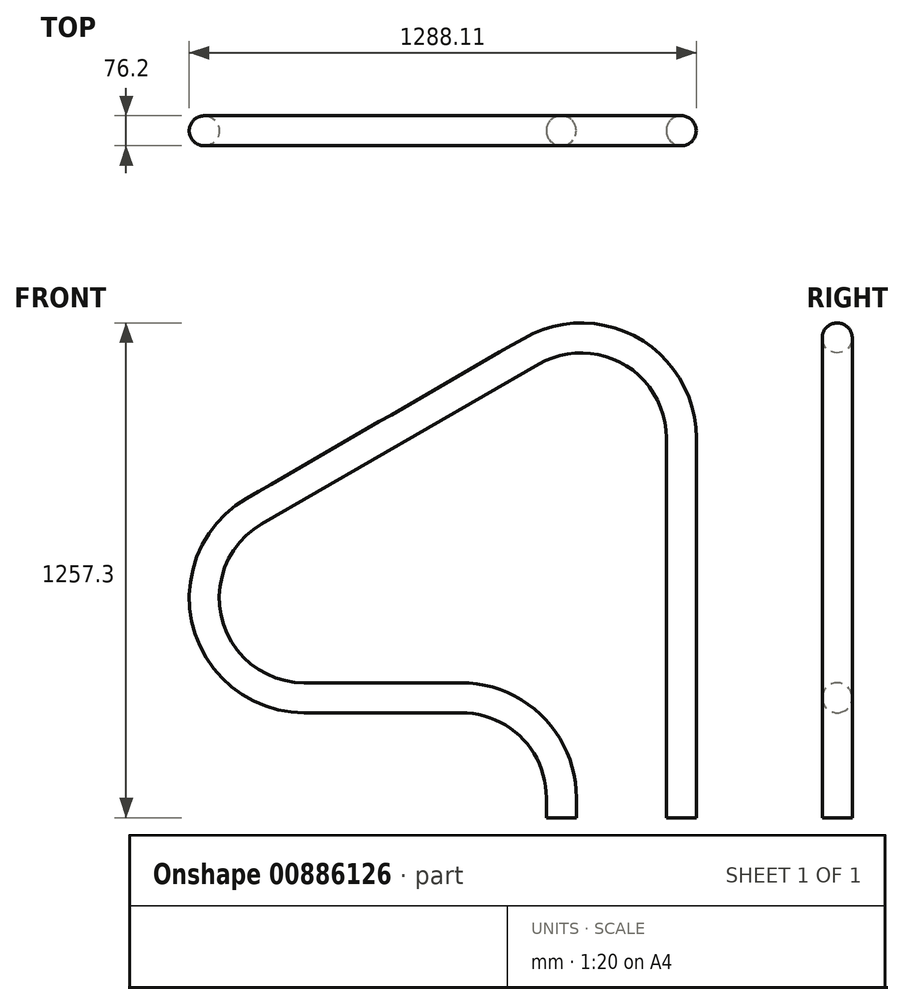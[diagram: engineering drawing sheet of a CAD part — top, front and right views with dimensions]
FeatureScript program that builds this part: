
annotation { "Feature Type Name" : "Feature", "Feature Type Description" : "" }
export const myFeature = defineFeature(function(context is Context, id is Id, definition is map)
    precondition{}
    {
        {
            var Q0;
            Q0=qCreatedBy(makeId("Front.planeOp"),FACE);
            var sketch = newSketch(context, id + "F0", { "sketchPlane" : qUnion([Q0])});
            skLineSegment(sketch, "E0", {"start": v(0, 0) * mm, "end": v(0, 965.2) * mm});
            skLineSegment(sketch, "E1", {"start": v(-381, 1185.17) * mm, "end": v(-1084.9, 778.77) * mm});
            skLineSegment(sketch, "E2", {"start": v(-957.9, 304.8) * mm, "end": v(-558.8, 304.8) * mm});
            skLineSegment(sketch, "E3", {"start": v(-304.8, 50.8) * mm, "end": v(-304.8, 0) * mm});
            skPoint(sketch, "E4.visualSharp", {"position": v(0, 1405.14) * mm});
            skArc(sketch, "E4.filletArc", {"start": v(0, 965.2) * mm, "mid": v(-127, 1185.17) * mm, "end": v(-381, 1185.17) * mm});
            skPoint(sketch, "E5.visualSharp", {"position": v(-1905.85, 304.8) * mm});
            skArc(sketch, "E5.filletArc", {"start": v(-1084.9, 778.77) * mm, "mid": v(-1203.25, 493.06) * mm, "end": v(-957.9, 304.8) * mm});
            skPoint(sketch, "E6.visualSharp", {"position": v(-304.8, 304.8) * mm});
            skArc(sketch, "E6.filletArc", {"start": v(-304.8, 50.8) * mm, "mid": v(-379.2, 230.4) * mm, "end": v(-558.8, 304.8) * mm});
            skLineSegment(sketch, "E7", {"start": v(-615.1, 1219.2) * mm, "end": v(-254, 1219.2) * mm, "construction": true});
            skSolve(sketch);
        }
        {
            var Q0;
            Q0=sQuery(id+"F0.wireOp",VERTEX,"E0.start");
            var Q1;
            Q1=sQuery(id+"F0.wireOp",EDGE,"E0");
            cPlane(context, id + "F1", {"entities" : qUnion([Q0, Q1]), "cplaneType" : CPlaneType.LINE_POINT, "offset" : 25.4 * mm, "width" : 152.4 * mm, "height" : 152.4 * mm});
        }
        {
            var Q0;
            Q0=qCreatedBy(id+"F1.planeOp",FACE);
            var sketch = newSketch(context, id + "F2", { "sketchPlane" : qUnion([Q0])});
            skCircle(sketch, "E8", {"center": v(0, 0) * mm, "radius": 38.1 * mm});
            skSolve(sketch);
        }
        {
            var Q0;
            Q0=makeQuery(id+"F2.imprint","IMPRINT",FACE,{"disambiguationData":[TD([[makeQuery(id+"F2.imprint","IMPRINT",EDGE,{"derivedFrom":sQuery(id+"F2.wireOp",EDGE,"E8")}),1.0]])]});
            var Q1;
            Q1 = qConstructionFilter(qBodyType(qCreatedBy(id + "F0" ,EDGE), BodyType.WIRE), ConstructionObject.NO);
            sweep(context, id + "F3", {"profiles" : qUnion([Q0]), "path" : qUnion([Q1])});
        }
    });
